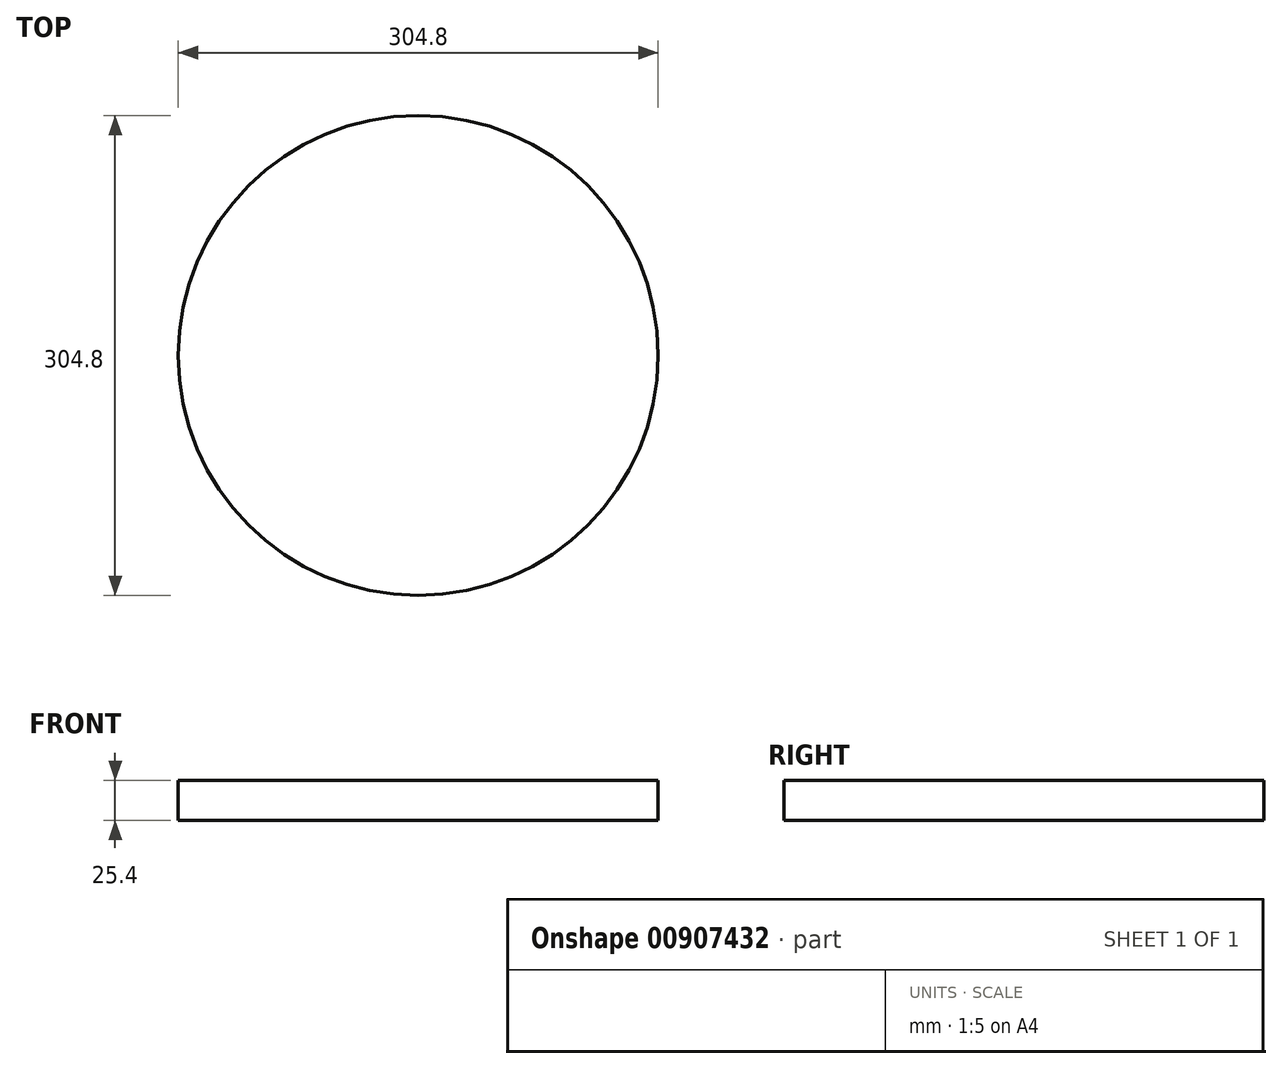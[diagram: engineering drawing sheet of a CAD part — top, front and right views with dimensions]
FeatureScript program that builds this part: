
annotation { "Feature Type Name" : "Feature", "Feature Type Description" : "" }
export const myFeature = defineFeature(function(context is Context, id is Id, definition is map)
    precondition{}
    {
        {
            var Q0;
            Q0=qCreatedBy(makeId("Top.planeOp"),FACE);
            var sketch = newSketch(context, id + "F0", { "sketchPlane" : qUnion([Q0])});
            skCircle(sketch, "E0", {"center": v(0, 0) * mm, "radius": 152.4 * mm});
            skSolve(sketch);
        }
        {
            var Q0;
            Q0=makeQuery(id+"F0.imprint","IMPRINT",FACE,{"disambiguationData":[TD([[makeQuery(id+"F0.imprint","IMPRINT",EDGE,{"derivedFrom":sQuery(id+"F0.wireOp",EDGE,"E0")}),1.0]])]});
            extrude(context, id + "F1", {"entities" : qUnion([Q0]), "depth" : 25.4 * mm, "offsetDistance" : 25.4 * mm});
        }
    });
